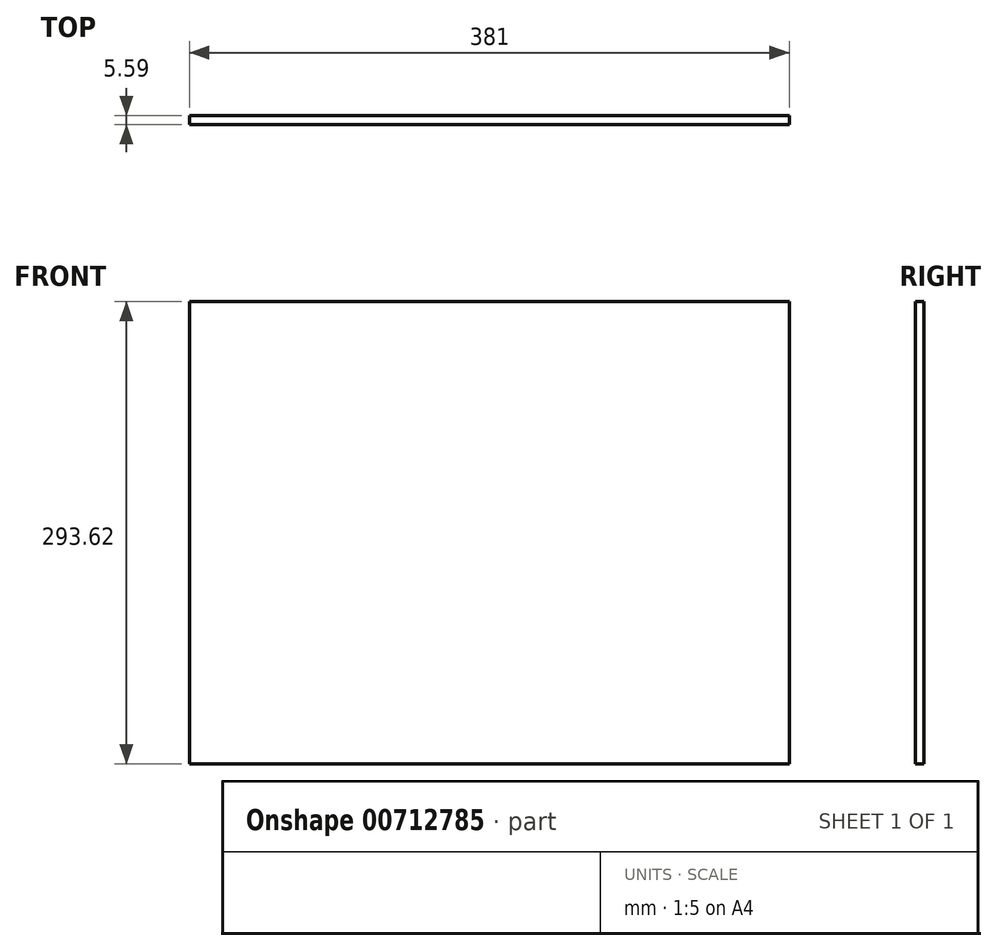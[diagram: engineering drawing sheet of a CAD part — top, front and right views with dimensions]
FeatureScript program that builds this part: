
annotation { "Feature Type Name" : "Feature", "Feature Type Description" : "" }
export const myFeature = defineFeature(function(context is Context, id is Id, definition is map)
    precondition{}
    {
        {
            var Q0;
            Q0=qCreatedBy(makeId("Front.planeOp"),FACE);
            var sketch = newSketch(context, id + "F0", { "sketchPlane" : qUnion([Q0])});
            skLineSegment(sketch, "E0.bottom", {"start": v(0, 0) * mm, "end": v(381, 0) * mm});
            skLineSegment(sketch, "E0.top", {"start": v(0, -293.62) * mm, "end": v(381, -293.62) * mm});
            skLineSegment(sketch, "E0.left", {"start": v(0, 0) * mm, "end": v(0, -293.62) * mm});
            skLineSegment(sketch, "E0.right", {"start": v(381, 0) * mm, "end": v(381, -293.62) * mm});
            skSolve(sketch);
        }
        {
            var Q0;
            Q0 = qSketchRegion(id + "F0", true);
            extrude(context, id + "F1", {"entities" : qUnion([Q0]), "depth" : 5.6 * mm, "offsetDistance" : 25.4 * mm});
        }
    });
